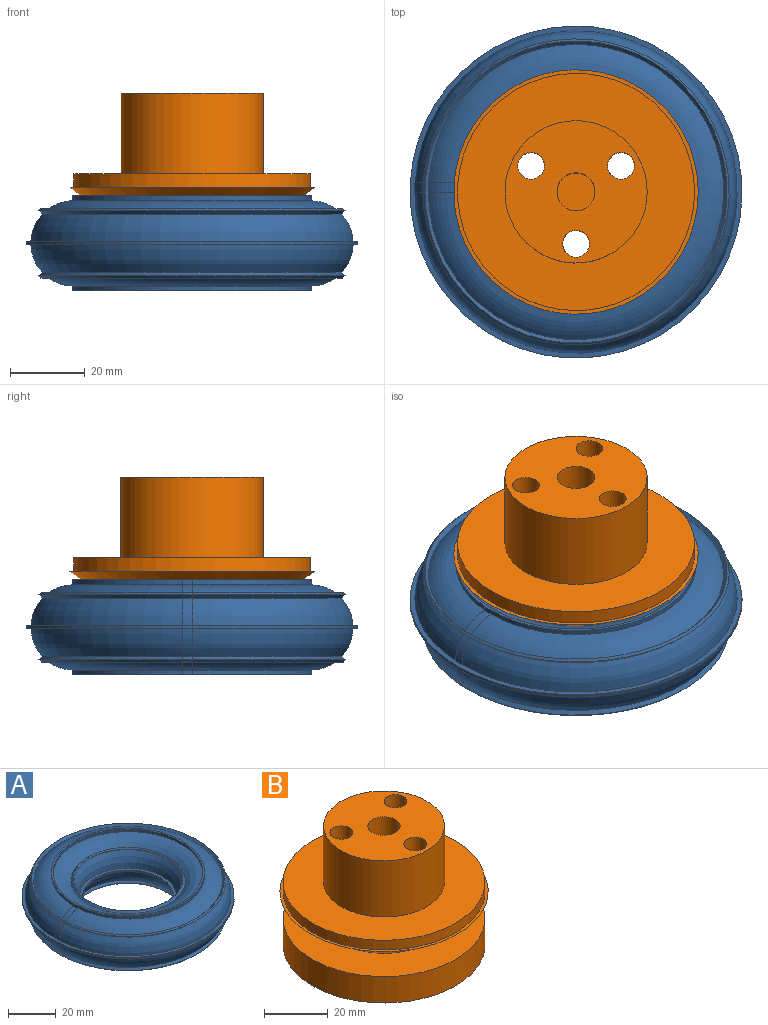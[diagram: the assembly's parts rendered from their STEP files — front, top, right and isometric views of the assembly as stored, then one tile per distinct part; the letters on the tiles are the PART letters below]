
ASSEMBLY  parts=2 mates=1
PART A: 56 faces, bbox 93.6x93.6x25.5 mm
  f0: cone r=23.39mm half-angle=45deg, axis (0,0,1), area 186.8mm2, adj f1,f31
  f1: torus R=31.75mm, axis (0,0,1), area 1101mm2, adj f0,f2
  f2: plane 40.65x40.65mm, normal (0,0,-1), area 160.3mm2, adj f1,f3
  f3: cylinder r=19.03mm len=38.06mm, axis (0,0,1), area 95mm2, adj f2,f4
  f4: plane 40.65x40.65mm, normal (0,0,1), area 160.3mm2, adj f3,f5
  f5: torus R=31.75mm, axis (0,0,1), area 1101mm2, adj f4,f6
  f6: cone r=23.39mm half-angle=45deg, axis (0,0,-1), area 186.8mm2, adj f5,f7
  f7: cone r=22.48mm half-angle=45deg, axis (0,0,1), area 113.6mm2, adj f6,f8
  f8: cone r=23.95mm half-angle=45deg, axis (0,0,-1), area 188.2mm2, adj f7,f9,f53,f54,f55
  f9: torus R=31.75mm, axis (0,0,1), area 1412.1mm2, adj f8,f10,f54,f55
  f10: cylinder r=31.35mm len=62.71mm, axis (0,0,1), area 255.4mm2, adj f9,f11
  f11: plane 64.29x64.29mm, normal (0,0,1), area 158.6mm2, adj f10,f12,f50,f52
  f12: cylinder r=32.15mm len=64.29mm, axis (0,0,1), area 258.6mm2, adj f11,f13,f50,f52
  f13: torus R=31.75mm, axis (0,0,1), area 1831.4mm2, adj f12,f14,f50,f51
  f14: cone r=39.55mm half-angle=45deg, axis (0,0,1), area 325.8mm2, adj f13,f15,f50,f51
  f15: cone r=40.46mm half-angle=45deg, axis (0,0,-1), area 201.4mm2, adj f14,f16,f45,f48,f49
  f16: cone r=40.11mm half-angle=45deg, axis (0,0,1), area 327.1mm2, adj f15,f17,f45,f47
  f17: torus R=31.75mm, axis (0,0,1), area 2142.7mm2, adj f16,f18,f45,f46
  f18: plane 88.94x88.94mm, normal (0,0,1), area 356.9mm2, adj f17,f19,f43,f44,f45,f46
  f19: cylinder r=44.47mm len=88.94mm, axis (0,0,1), area 219.9mm2, adj f18,f20,f43,f44
  f20: plane 88.94x88.94mm, normal (0,0,-1), area 356.9mm2, adj f19,f21,f39,f42,f43,f44
  f21: torus R=31.75mm, axis (0,0,1), area 2142.7mm2, adj f20,f22,f39,f42
  f22: cone r=40.11mm half-angle=45deg, axis (0,0,-1), area 327.1mm2, adj f21,f23,f39,f41
  f23: cone r=41.02mm half-angle=45deg, axis (0,0,1), area 201.4mm2, adj f22,f24,f38,f39,f40
  f24: cone r=39.55mm half-angle=45deg, axis (0,0,-1), area 325.8mm2, adj f23,f25,f36,f37
  f25: torus R=31.75mm, axis (0,0,1), area 1831.4mm2, adj f24,f26,f36,f37
  f26: cylinder r=32.15mm len=64.29mm, axis (0,0,1), area 258.6mm2, adj f25,f27,f35,f36
  f27: plane 64.29x64.29mm, normal (0,0,-1), area 158.6mm2, adj f26,f28,f35,f36
  f28: cylinder r=31.35mm len=62.71mm, axis (0,0,1), area 255.4mm2, adj f27,f29
  f29: torus R=31.75mm, axis (0,0,1), area 1412.1mm2, adj f28,f30,f32,f33
  f30: cone r=23.95mm half-angle=45deg, axis (0,0,1), area 188.2mm2, adj f29,f31,f32,f33,f34
  f31: cone r=23.04mm half-angle=45deg, axis (0,0,-1), area 113.6mm2, adj f0,f30
  f32: plane 2.59x0.96mm, normal (-0.71,0,-0.71), area 3.2mm2, adj f29,f30,f33,f34
  f33: plane 0.92x0.92mm, normal (0,-1,0), area 0.1mm2, adj f29,f30,f32,f34
  f34: plane 2.59x0.12mm, normal (0.71,0,-0.71), area 0.1mm2, adj f30,f32,f33
  f35: plane 2.54x1.3mm, normal (-1,0,0), area 3.3mm2, adj f26,f27,f36,f37
  f36: plane 7.55x4.46mm, normal (0,-1,0), area 0.4mm2, adj f24,f25,f26,f27,f35,f37
  f37: cylinder r=11.43mm len=7.4mm, axis (0,1,0), area 20.7mm2, adj f24,f25,f35,f36
  f38: plane 2.54x0.56mm, normal (-0.71,0,-0.71), area 2mm2, adj f23,f39,f40,f41
  f39: plane 8.97x3.24mm, normal (0,-1,0), area 0.7mm2, adj f20,f21,f22,f23,f38,f40,f41,f42
  f40: plane 2.57x0.07mm, normal (0.71,0,-0.71), area 0mm2, adj f23,f38,f39
  f41: plane 2.54x0.92mm, normal (-0.71,0,0.71), area 3.3mm2, adj f22,f38,f39,f42
  f42: cylinder r=11.43mm len=7.4mm, axis (0,1,0), area 20.8mm2, adj f20,f21,f39,f41
  f43: plane 2.54x0.79mm, normal (-1,0,0), area 2mm2, adj f18,f19,f20,f44
  f44: plane 0.79x0.07mm, normal (0,-1,0), area 0.1mm2, adj f18,f19,f20,f43
  f45: plane 8.97x3.24mm, normal (0,-1,0), area 0.7mm2, adj f15,f16,f17,f18,f46,f47,f48,f49
  f46: cylinder r=11.43mm len=7.4mm, axis (0,1,0), area 20.8mm2, adj f17,f18,f45,f47
  f47: plane 2.54x0.92mm, normal (-0.71,0,-0.71), area 3.3mm2, adj f16,f45,f46,f48
  f48: plane 2.54x0.56mm, normal (-0.71,0,0.71), area 2mm2, adj f15,f45,f47,f49
  f49: plane 2.57x0.07mm, normal (0.71,0,0.71), area 0mm2, adj f15,f45,f48
  f50: plane 7.56x4.46mm, normal (0,-1,0), area 0.4mm2, adj f11,f12,f13,f14,f51,f52
  f51: cylinder r=11.43mm len=7.4mm, axis (0,1,0), area 20.7mm2, adj f13,f14,f50,f52
  f52: plane 2.54x1.3mm, normal (-1,0,0), area 3.3mm2, adj f11,f12,f50,f51
  f53: plane 2.59x0.12mm, normal (0.71,0,0.71), area 0.1mm2, adj f8,f54,f55
  f54: plane 0.92x0.92mm, normal (0,-1,0), area 0.1mm2, adj f8,f9,f53,f55
  f55: plane 2.59x0.97mm, normal (-0.71,0,0.71), area 3.2mm2, adj f8,f9,f53,f54
PART B: 15 faces, bbox 65.5x65.5x49.7 mm
  f0: plane 63.5x63.5mm, normal (0,0,-1), area 2863.9mm2, adj f1,f9,f10,f11,f12
  f1: cone r=7.59mm half-angle=62.6deg, axis (0,0,1), area 204mm2, adj f0
  f2: plane 38.1x38.1mm, normal (0,0,1), area 937.2mm2, adj f3,f10,f11,f12,f13
  f3: cylinder r=19.05mm len=38.1mm, axis (0,0,1), area 2582.6mm2, adj f2,f4
  f4: plane 63.5x63.5mm, normal (0,0,1), area 2026.8mm2, adj f3,f5
  f5: cylinder r=31.75mm len=63.5mm, axis (0,0,1), area 731.3mm2, adj f4,f6
  f6: plane 65.48x65.48mm, normal (0,0,1), area 200.9mm2, adj f5,f7
  f7: cone r=32.74mm half-angle=53deg, axis (0,0,1), area 2789.4mm2, adj f6,f8
  f8: plane 63.5x63.5mm, normal (0,0,1), area 2026.8mm2, adj f7,f9
  f9: cylinder r=31.75mm len=63.5mm, axis (0,0,1), area 2026.8mm2, adj f0,f8
  f10: cylinder r=3.59mm len=45.72mm, axis (0,0,-1), area 1032.7mm2, adj f0,f2
  f11: cylinder r=3.59mm len=45.72mm, axis (0,0,-1), area 1032.7mm2, adj f0,f2
  f12: cylinder r=3.59mm len=45.72mm, axis (0,0,-1), area 1032.7mm2, adj f0,f2
  f13: cylinder r=5.08mm len=25.4mm, axis (0,0,1), area 810.7mm2, adj f2,f14
  f14: plane 10.16x10.16mm, normal (0,0,1), area 81.1mm2, adj f13
PLACE A rot(axis=(1,0,0),180deg) t=(25.7,36.13,69.36)mm
PLACE B t=(25.7,36.13,109.61)mm
MATE fastened B.f1 <-> A.f0  axis (0,0,1) through (25.7,36.13,68.97)mm
